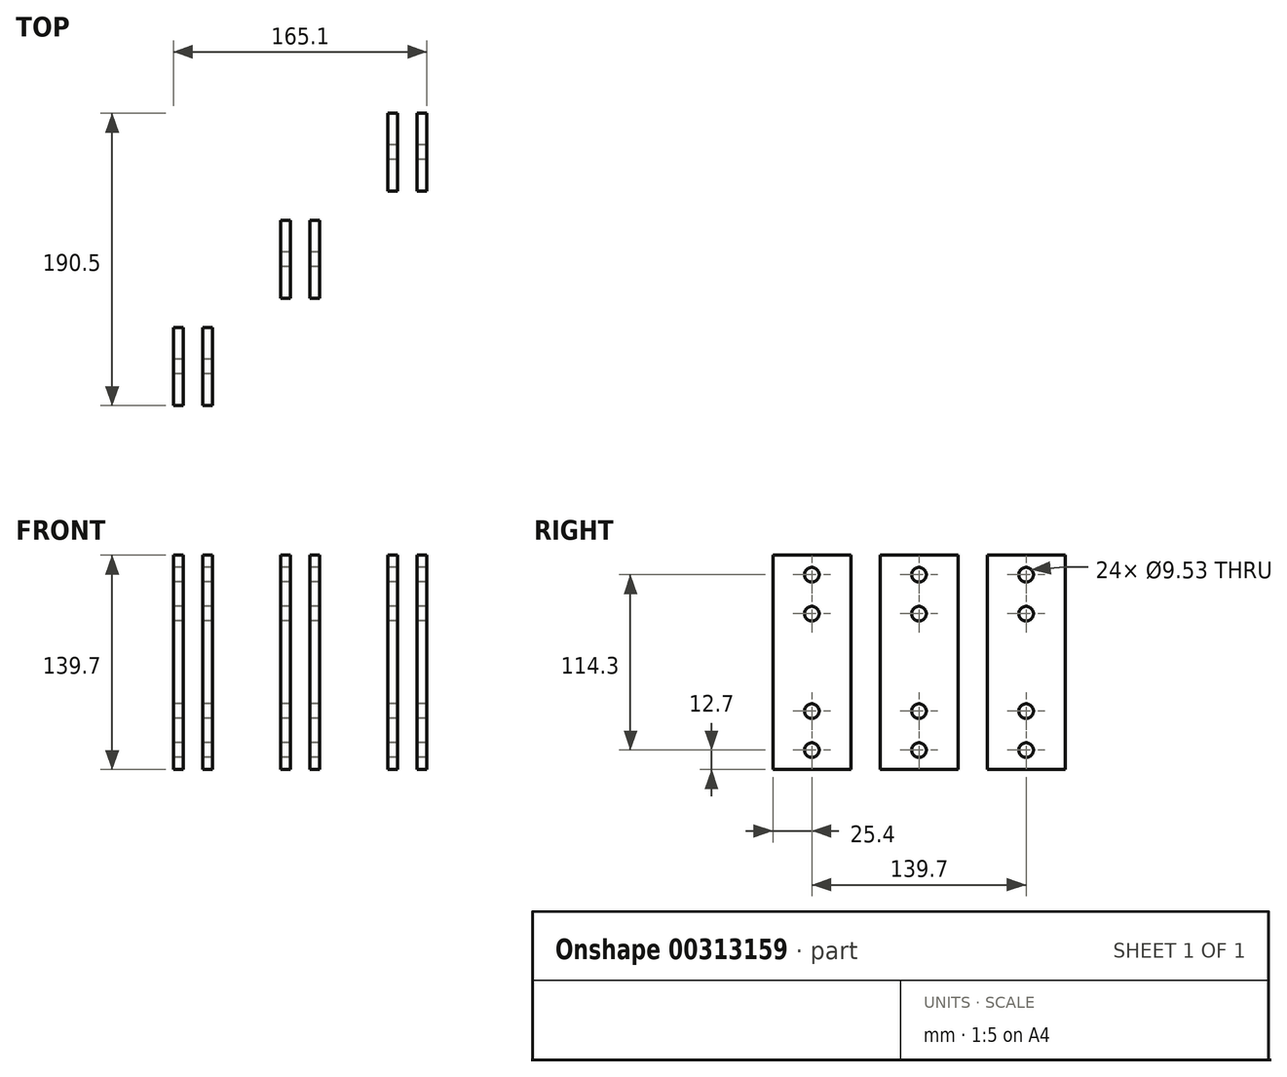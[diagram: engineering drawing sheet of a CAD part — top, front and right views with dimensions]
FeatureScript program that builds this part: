
annotation { "Feature Type Name" : "Feature", "Feature Type Description" : "" }
export const myFeature = defineFeature(function(context is Context, id is Id, definition is map)
    precondition{}
    {
        {
            var Q0;
            Q0=qCreatedBy(makeId("Top.planeOp"),FACE);
            var sketch = newSketch(context, id + "F0", { "sketchPlane" : qUnion([Q0])});
            skLineSegment(sketch, "E0.bottom", {"start": v(0, 50.8) * mm, "end": v(6.35, 50.8) * mm});
            skLineSegment(sketch, "E0.top", {"start": v(0, 0) * mm, "end": v(6.35, 0) * mm});
            skLineSegment(sketch, "E0.left", {"start": v(0, 50.8) * mm, "end": v(0, 0) * mm});
            skLineSegment(sketch, "E0.right", {"start": v(6.35, 50.8) * mm, "end": v(6.35, 0) * mm});
            skLineSegment(sketch, "E1.bottom", {"start": v(19.05, 50.8) * mm, "end": v(25.4, 50.8) * mm});
            skLineSegment(sketch, "E1.top", {"start": v(19.05, 0) * mm, "end": v(25.4, 0) * mm});
            skLineSegment(sketch, "E1.left", {"start": v(19.05, 50.8) * mm, "end": v(19.05, 0) * mm});
            skLineSegment(sketch, "E1.right", {"start": v(25.4, 50.8) * mm, "end": v(25.4, 0) * mm});
            skLineSegment(sketch, "E2.bottom", {"start": v(-69.85, -19.05) * mm, "end": v(-63.5, -19.05) * mm});
            skLineSegment(sketch, "E2.top", {"start": v(-69.85, -69.85) * mm, "end": v(-63.5, -69.85) * mm});
            skLineSegment(sketch, "E2.left", {"start": v(-69.85, -19.05) * mm, "end": v(-69.85, -69.85) * mm});
            skLineSegment(sketch, "E2.right", {"start": v(-63.5, -19.05) * mm, "end": v(-63.5, -69.85) * mm});
            skLineSegment(sketch, "E3.bottom", {"start": v(-50.8, -19.05) * mm, "end": v(-44.45, -19.05) * mm});
            skLineSegment(sketch, "E3.top", {"start": v(-50.8, -69.85) * mm, "end": v(-44.45, -69.85) * mm});
            skLineSegment(sketch, "E3.left", {"start": v(-50.8, -19.05) * mm, "end": v(-50.8, -69.85) * mm});
            skLineSegment(sketch, "E3.right", {"start": v(-44.45, -19.05) * mm, "end": v(-44.45, -69.85) * mm});
            skLineSegment(sketch, "E4.bottom", {"start": v(-139.7, -88.9) * mm, "end": v(-133.35, -88.9) * mm});
            skLineSegment(sketch, "E4.top", {"start": v(-139.7, -139.7) * mm, "end": v(-133.35, -139.7) * mm});
            skLineSegment(sketch, "E4.left", {"start": v(-139.7, -88.9) * mm, "end": v(-139.7, -139.7) * mm});
            skLineSegment(sketch, "E4.right", {"start": v(-133.35, -88.9) * mm, "end": v(-133.35, -139.7) * mm});
            skLineSegment(sketch, "E5.bottom", {"start": v(-120.65, -88.9) * mm, "end": v(-114.3, -88.9) * mm});
            skLineSegment(sketch, "E5.top", {"start": v(-120.65, -139.7) * mm, "end": v(-114.3, -139.7) * mm});
            skLineSegment(sketch, "E5.left", {"start": v(-120.65, -88.9) * mm, "end": v(-120.65, -139.7) * mm});
            skLineSegment(sketch, "E5.right", {"start": v(-114.3, -88.9) * mm, "end": v(-114.3, -139.7) * mm});
            skSolve(sketch);
        }
        {
            var Q0;
            Q0 = qSketchRegion(id + "F0", true);
            extrude(context, id + "F1", {"entities" : qUnion([Q0]), "endBound" : BoundingType.SYMMETRIC, "depth" : 139.7 * mm});
        }
        {
            var Q0;
            Q0=makeQuery(id+"F1.opExtrude","SWEPT_FACE",FACE,{"disambiguationData":[OSD([sQuery(id+"F0.wireOp",EDGE,"E4.left")])]});
            var sketch = newSketch(context, id + "F2", { "sketchPlane" : qUnion([Q0])});
            skCircle(sketch, "E6", {"center": v(114.3, 57.15) * mm, "radius": 4.76 * mm});
            skCircle(sketch, "E7", {"center": v(114.3, 31.75) * mm, "radius": 4.76 * mm});
            skCircle(sketch, "E8.0.1.0", {"center": v(114.3, -57.15) * mm, "radius": 4.76 * mm});
            skCircle(sketch, "E8.0.1.1", {"center": v(114.3, -31.75) * mm, "radius": 4.76 * mm});
            skCircle(sketch, "E8.1.0.0", {"center": v(44.45, 31.75) * mm, "radius": 4.76 * mm});
            skCircle(sketch, "E8.1.0.1", {"center": v(44.45, 57.15) * mm, "radius": 4.76 * mm});
            skCircle(sketch, "E8.1.1.0", {"center": v(44.45, -57.15) * mm, "radius": 4.76 * mm});
            skCircle(sketch, "E8.1.1.1", {"center": v(44.45, -31.75) * mm, "radius": 4.76 * mm});
            skCircle(sketch, "E8.2.0.0", {"center": v(-25.4, 31.75) * mm, "radius": 4.76 * mm});
            skCircle(sketch, "E8.2.0.1", {"center": v(-25.4, 57.15) * mm, "radius": 4.76 * mm});
            skCircle(sketch, "E8.2.1.0", {"center": v(-25.4, -57.15) * mm, "radius": 4.76 * mm});
            skCircle(sketch, "E8.2.1.1", {"center": v(-25.4, -31.75) * mm, "radius": 4.76 * mm});
            skLineSegment(sketch, "E8.direction1", {"start": v(114.3, 31.75) * mm, "end": v(44.45, 31.75) * mm, "construction": true});
            skLineSegment(sketch, "E8.direction2", {"start": v(114.3, -57.15) * mm, "end": v(114.3, 31.75) * mm, "construction": true});
            skSolve(sketch);
        }
        {
            var Q0;
            Q0 = qSketchRegion(id + "F2", true);
            extrude(context, id + "F3", {"entities" : qUnion([Q0]), "operationType" : NewBodyOperationType.REMOVE, "endBound" : BoundingType.THROUGH_ALL, "oppositeDirection" : true, "depth" : 25.4 * mm});
        }
    });
